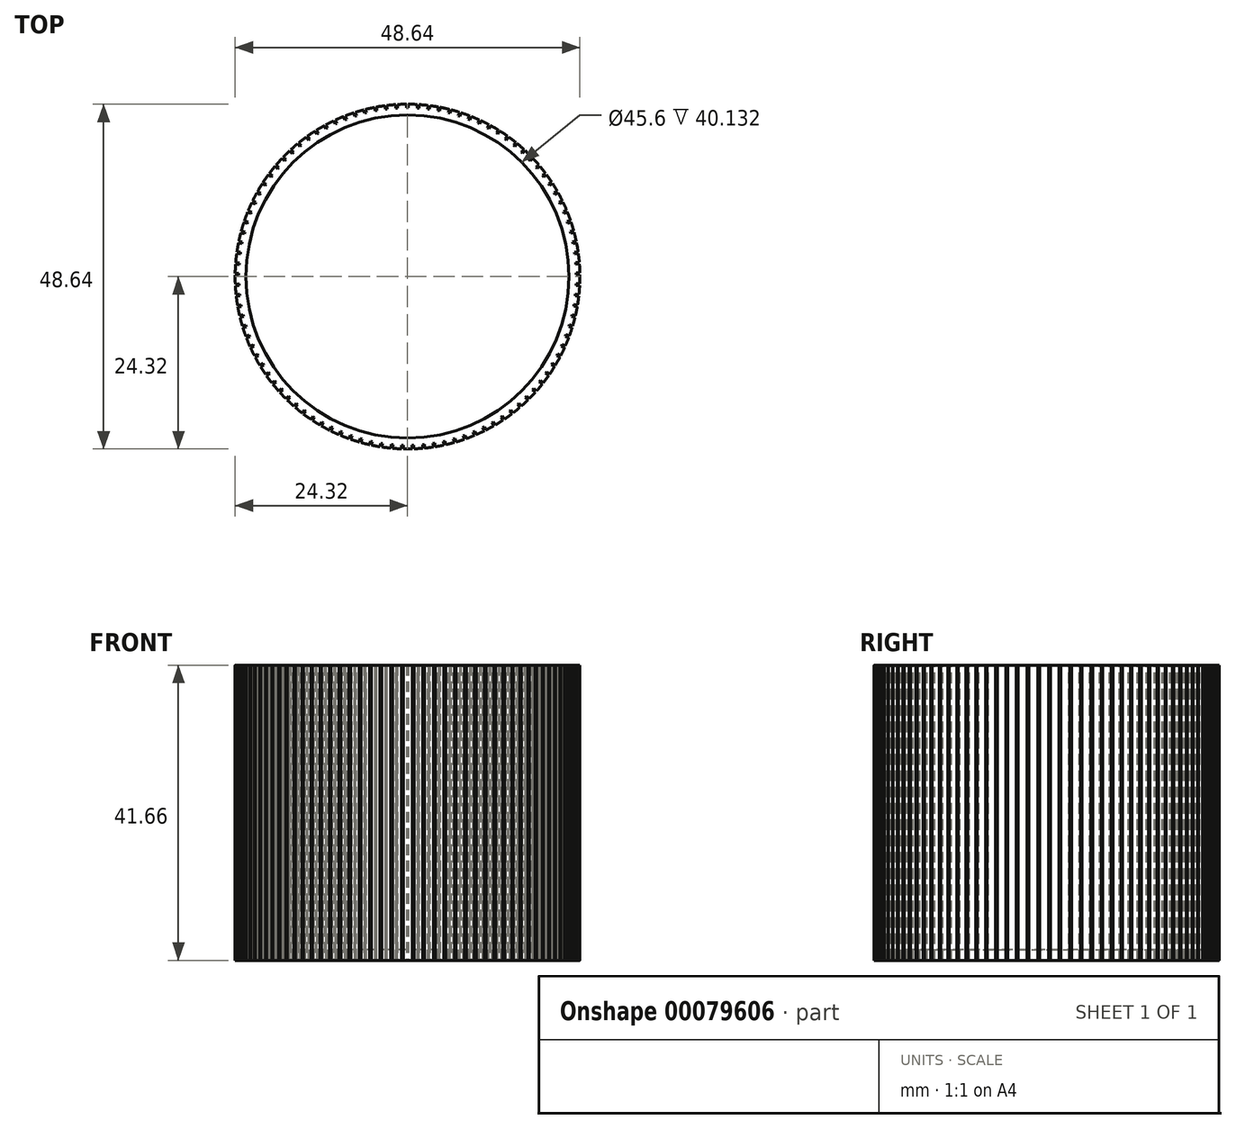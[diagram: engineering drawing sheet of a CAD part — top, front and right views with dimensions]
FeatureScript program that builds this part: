
annotation { "Feature Type Name" : "Feature", "Feature Type Description" : "" }
export const myFeature = defineFeature(function(context is Context, id is Id, definition is map)
    precondition{}
    {
        {
            var Q0;
            Q0=qCreatedBy(makeId("Top.planeOp"),FACE);
            var sketch = newSketch(context, id + "F0", { "sketchPlane" : qUnion([Q0])});
            skCircle(sketch, "E0", {"center": v(0, 0) * mm, "radius": 24.32 * mm});
            skSolve(sketch);
        }
        {
            var Q0;
            Q0 = qSketchRegion(id + "F0", true);
            extrude(context, id + "F1", {"entities" : qUnion([Q0]), "depth" : 41.66 * mm});
        }
        {
            var Q0;
            Q0=makeQuery(id+"F1.opExtrude","CAP_FACE",FACE,{"disambiguationData":[OSD([sQuery(id+"F0.wireOp",EDGE,"E0")])],"isStart":false});
            shell(context, id + "F2", {"entities" : qUnion([Q0]), "thickness" : 1.52 * mm});
        }
        {
            var Q0;
            Q0=makeQuery(id+"F1.opExtrude","CAP_FACE",FACE,{"disambiguationData":[OSD([sQuery(id+"F0.wireOp",EDGE,"E0")])],"isStart":false});
            var sketch = newSketch(context, id + "F3", { "sketchPlane" : qUnion([Q0])});
            skLineSegment(sketch, "E1.left", {"start": v(-0.13, 25.12) * mm, "end": v(-0.13, 23.82) * mm});
            skLineSegment(sketch, "E1.right", {"start": v(0.13, 25.12) * mm, "end": v(0.13, 23.82) * mm});
            skLineSegment(sketch, "E2.1.0", {"start": v(1.43, 25.08) * mm, "end": v(1.35, 23.78) * mm});
            skLineSegment(sketch, "E2.1.1", {"start": v(1.69, 25.07) * mm, "end": v(1.6, 23.76) * mm});
            skLineSegment(sketch, "E2.1.2", {"start": v(1.35, 23.78) * mm, "end": v(1.6, 23.76) * mm});
            skLineSegment(sketch, "E2.1.3", {"start": v(1.43, 25.08) * mm, "end": v(1.69, 25.07) * mm});
            skLineSegment(sketch, "E2.2.0", {"start": v(3, 24.94) * mm, "end": v(2.83, 23.65) * mm});
            skLineSegment(sketch, "E2.2.1", {"start": v(3.24, 24.91) * mm, "end": v(3.08, 23.62) * mm});
            skLineSegment(sketch, "E2.2.2", {"start": v(2.83, 23.65) * mm, "end": v(3.08, 23.62) * mm});
            skLineSegment(sketch, "E2.2.3", {"start": v(3, 24.94) * mm, "end": v(3.24, 24.91) * mm});
            skLineSegment(sketch, "E2.3.0", {"start": v(4.54, 24.7) * mm, "end": v(4.3, 23.43) * mm});
            skLineSegment(sketch, "E2.3.1", {"start": v(4.78, 24.66) * mm, "end": v(4.54, 23.38) * mm});
            skLineSegment(sketch, "E2.3.2", {"start": v(4.3, 23.43) * mm, "end": v(4.54, 23.38) * mm});
            skLineSegment(sketch, "E2.3.3", {"start": v(4.54, 24.7) * mm, "end": v(4.78, 24.66) * mm});
            skLineSegment(sketch, "E2.4.0", {"start": v(6.06, 24.38) * mm, "end": v(5.74, 23.11) * mm});
            skLineSegment(sketch, "E2.4.1", {"start": v(6.3, 24.32) * mm, "end": v(5.99, 23.05) * mm});
            skLineSegment(sketch, "E2.4.2", {"start": v(5.74, 23.11) * mm, "end": v(5.99, 23.05) * mm});
            skLineSegment(sketch, "E2.4.3", {"start": v(6.06, 24.38) * mm, "end": v(6.3, 24.32) * mm});
            skLineSegment(sketch, "E2.5.0", {"start": v(7.57, 23.96) * mm, "end": v(7.17, 22.71) * mm});
            skLineSegment(sketch, "E2.5.1", {"start": v(7.8, 23.88) * mm, "end": v(7.4, 22.63) * mm});
            skLineSegment(sketch, "E2.5.2", {"start": v(7.17, 22.71) * mm, "end": v(7.4, 22.63) * mm});
            skLineSegment(sketch, "E2.5.3", {"start": v(7.57, 23.96) * mm, "end": v(7.8, 23.88) * mm});
            skLineSegment(sketch, "E2.6.0", {"start": v(9.04, 23.44) * mm, "end": v(8.56, 22.22) * mm});
            skLineSegment(sketch, "E2.6.1", {"start": v(9.28, 23.35) * mm, "end": v(8.8, 22.13) * mm});
            skLineSegment(sketch, "E2.6.2", {"start": v(8.56, 22.22) * mm, "end": v(8.8, 22.13) * mm});
            skLineSegment(sketch, "E2.6.3", {"start": v(9.04, 23.44) * mm, "end": v(9.28, 23.35) * mm});
            skLineSegment(sketch, "E2.7.0", {"start": v(10.48, 22.83) * mm, "end": v(9.93, 21.65) * mm});
            skLineSegment(sketch, "E2.7.1", {"start": v(10.7, 22.73) * mm, "end": v(10.16, 21.54) * mm});
            skLineSegment(sketch, "E2.7.2", {"start": v(9.93, 21.65) * mm, "end": v(10.16, 21.54) * mm});
            skLineSegment(sketch, "E2.7.3", {"start": v(10.48, 22.83) * mm, "end": v(10.7, 22.73) * mm});
            skLineSegment(sketch, "E2.8.0", {"start": v(11.88, 22.14) * mm, "end": v(11.25, 20.99) * mm});
            skLineSegment(sketch, "E2.8.1", {"start": v(12.1, 22.02) * mm, "end": v(11.48, 20.87) * mm});
            skLineSegment(sketch, "E2.8.2", {"start": v(11.25, 20.99) * mm, "end": v(11.48, 20.87) * mm});
            skLineSegment(sketch, "E2.8.3", {"start": v(11.88, 22.14) * mm, "end": v(12.1, 22.02) * mm});
            skLineSegment(sketch, "E2.9.0", {"start": v(13.23, 21.36) * mm, "end": v(12.54, 20.25) * mm});
            skLineSegment(sketch, "E2.9.1", {"start": v(13.45, 21.22) * mm, "end": v(12.75, 20.11) * mm});
            skLineSegment(sketch, "E2.9.2", {"start": v(12.54, 20.25) * mm, "end": v(12.75, 20.11) * mm});
            skLineSegment(sketch, "E2.9.3", {"start": v(13.23, 21.36) * mm, "end": v(13.45, 21.22) * mm});
            skLineSegment(sketch, "E2.10.0", {"start": v(14.53, 20.5) * mm, "end": v(13.77, 19.43) * mm});
            skLineSegment(sketch, "E2.10.1", {"start": v(14.74, 20.34) * mm, "end": v(13.98, 19.28) * mm});
            skLineSegment(sketch, "E2.10.2", {"start": v(13.77, 19.43) * mm, "end": v(13.98, 19.28) * mm});
            skLineSegment(sketch, "E2.10.3", {"start": v(14.53, 20.5) * mm, "end": v(14.74, 20.34) * mm});
            skLineSegment(sketch, "E2.11.0", {"start": v(15.78, 19.55) * mm, "end": v(14.95, 18.54) * mm});
            skLineSegment(sketch, "E2.11.1", {"start": v(15.98, 19.39) * mm, "end": v(15.15, 18.38) * mm});
            skLineSegment(sketch, "E2.11.2", {"start": v(14.95, 18.54) * mm, "end": v(15.15, 18.38) * mm});
            skLineSegment(sketch, "E2.11.3", {"start": v(15.78, 19.55) * mm, "end": v(15.98, 19.39) * mm});
            skLineSegment(sketch, "E2.12.0", {"start": v(16.96, 18.53) * mm, "end": v(16.08, 17.57) * mm});
            skLineSegment(sketch, "E2.12.1", {"start": v(17.15, 18.36) * mm, "end": v(16.26, 17.4) * mm});
            skLineSegment(sketch, "E2.12.2", {"start": v(16.08, 17.57) * mm, "end": v(16.26, 17.4) * mm});
            skLineSegment(sketch, "E2.12.3", {"start": v(16.96, 18.53) * mm, "end": v(17.15, 18.36) * mm});
            skLineSegment(sketch, "E2.13.0", {"start": v(18.08, 17.44) * mm, "end": v(17.14, 16.54) * mm});
            skLineSegment(sketch, "E2.13.1", {"start": v(18.26, 17.26) * mm, "end": v(17.31, 16.35) * mm});
            skLineSegment(sketch, "E2.13.2", {"start": v(17.14, 16.54) * mm, "end": v(17.31, 16.35) * mm});
            skLineSegment(sketch, "E2.13.3", {"start": v(18.08, 17.44) * mm, "end": v(18.26, 17.26) * mm});
            skLineSegment(sketch, "E2.14.0", {"start": v(19.13, 16.28) * mm, "end": v(18.13, 15.44) * mm});
            skLineSegment(sketch, "E2.14.1", {"start": v(19.3, 16.09) * mm, "end": v(18.3, 15.25) * mm});
            skLineSegment(sketch, "E2.14.2", {"start": v(18.13, 15.44) * mm, "end": v(18.3, 15.25) * mm});
            skLineSegment(sketch, "E2.14.3", {"start": v(19.13, 16.28) * mm, "end": v(19.3, 16.09) * mm});
            skLineSegment(sketch, "E2.15.0", {"start": v(20.1, 15.06) * mm, "end": v(19.06, 14.28) * mm});
            skLineSegment(sketch, "E2.15.1", {"start": v(20.26, 14.86) * mm, "end": v(19.2, 14.08) * mm});
            skLineSegment(sketch, "E2.15.2", {"start": v(19.06, 14.28) * mm, "end": v(19.2, 14.08) * mm});
            skLineSegment(sketch, "E2.15.3", {"start": v(20.1, 15.06) * mm, "end": v(20.26, 14.86) * mm});
            skLineSegment(sketch, "E2.16.0", {"start": v(21, 13.78) * mm, "end": v(19.9, 13.07) * mm});
            skLineSegment(sketch, "E2.16.1", {"start": v(21.14, 13.57) * mm, "end": v(20.05, 12.86) * mm});
            skLineSegment(sketch, "E2.16.2", {"start": v(19.9, 13.07) * mm, "end": v(20.05, 12.86) * mm});
            skLineSegment(sketch, "E2.16.3", {"start": v(21, 13.78) * mm, "end": v(21.14, 13.57) * mm});
            skLineSegment(sketch, "E2.17.0", {"start": v(21.82, 12.45) * mm, "end": v(20.68, 11.8) * mm});
            skLineSegment(sketch, "E2.17.1", {"start": v(21.94, 12.23) * mm, "end": v(20.8, 11.59) * mm});
            skLineSegment(sketch, "E2.17.2", {"start": v(20.68, 11.8) * mm, "end": v(20.8, 11.59) * mm});
            skLineSegment(sketch, "E2.17.3", {"start": v(21.82, 12.45) * mm, "end": v(21.94, 12.23) * mm});
            skLineSegment(sketch, "E2.18.0", {"start": v(22.55, 11.07) * mm, "end": v(21.37, 10.5) * mm});
            skLineSegment(sketch, "E2.18.1", {"start": v(22.66, 10.84) * mm, "end": v(21.49, 10.27) * mm});
            skLineSegment(sketch, "E2.18.2", {"start": v(21.37, 10.5) * mm, "end": v(21.49, 10.27) * mm});
            skLineSegment(sketch, "E2.18.3", {"start": v(22.55, 11.07) * mm, "end": v(22.66, 10.84) * mm});
            skLineSegment(sketch, "E2.19.0", {"start": v(23.2, 9.65) * mm, "end": v(21.99, 9.15) * mm});
            skLineSegment(sketch, "E2.19.1", {"start": v(23.3, 9.41) * mm, "end": v(22.08, 8.92) * mm});
            skLineSegment(sketch, "E2.19.2", {"start": v(21.99, 9.15) * mm, "end": v(22.08, 8.92) * mm});
            skLineSegment(sketch, "E2.19.3", {"start": v(23.2, 9.65) * mm, "end": v(23.3, 9.41) * mm});
            skLineSegment(sketch, "E2.20.0", {"start": v(23.75, 8.19) * mm, "end": v(22.51, 7.77) * mm});
            skLineSegment(sketch, "E2.20.1", {"start": v(23.83, 7.95) * mm, "end": v(22.6, 7.53) * mm});
            skLineSegment(sketch, "E2.20.2", {"start": v(22.51, 7.77) * mm, "end": v(22.6, 7.53) * mm});
            skLineSegment(sketch, "E2.20.3", {"start": v(23.75, 8.19) * mm, "end": v(23.83, 7.95) * mm});
            skLineSegment(sketch, "E2.21.0", {"start": v(24.21, 6.7) * mm, "end": v(22.95, 6.35) * mm});
            skLineSegment(sketch, "E2.21.1", {"start": v(24.28, 6.45) * mm, "end": v(23.02, 6.1) * mm});
            skLineSegment(sketch, "E2.21.2", {"start": v(22.95, 6.35) * mm, "end": v(23.02, 6.1) * mm});
            skLineSegment(sketch, "E2.21.3", {"start": v(24.21, 6.7) * mm, "end": v(24.28, 6.45) * mm});
            skLineSegment(sketch, "E2.22.0", {"start": v(24.58, 5.18) * mm, "end": v(23.3, 4.92) * mm});
            skLineSegment(sketch, "E2.22.1", {"start": v(24.63, 4.93) * mm, "end": v(23.35, 4.67) * mm});
            skLineSegment(sketch, "E2.22.2", {"start": v(23.3, 4.92) * mm, "end": v(23.35, 4.67) * mm});
            skLineSegment(sketch, "E2.22.3", {"start": v(24.58, 5.18) * mm, "end": v(24.63, 4.93) * mm});
            skLineSegment(sketch, "E2.23.0", {"start": v(24.86, 3.64) * mm, "end": v(23.56, 3.46) * mm});
            skLineSegment(sketch, "E2.23.1", {"start": v(24.9, 3.39) * mm, "end": v(23.6, 3.2) * mm});
            skLineSegment(sketch, "E2.23.2", {"start": v(23.56, 3.46) * mm, "end": v(23.6, 3.2) * mm});
            skLineSegment(sketch, "E2.23.3", {"start": v(24.86, 3.64) * mm, "end": v(24.9, 3.39) * mm});
            skLineSegment(sketch, "E2.24.0", {"start": v(25.04, 2.09) * mm, "end": v(23.73, 1.99) * mm});
            skLineSegment(sketch, "E2.24.1", {"start": v(25.06, 1.84) * mm, "end": v(23.75, 1.73) * mm});
            skLineSegment(sketch, "E2.24.2", {"start": v(23.73, 1.99) * mm, "end": v(23.75, 1.73) * mm});
            skLineSegment(sketch, "E2.24.3", {"start": v(25.04, 2.09) * mm, "end": v(25.06, 1.84) * mm});
            skLineSegment(sketch, "E2.25.0", {"start": v(25.12, 0.53) * mm, "end": v(23.8, 0.5) * mm});
            skLineSegment(sketch, "E2.25.1", {"start": v(25.12, 0.27) * mm, "end": v(23.81, 0.25) * mm});
            skLineSegment(sketch, "E2.25.2", {"start": v(23.8, 0.5) * mm, "end": v(23.81, 0.25) * mm});
            skLineSegment(sketch, "E2.25.3", {"start": v(25.12, 0.53) * mm, "end": v(25.12, 0.27) * mm});
            skLineSegment(sketch, "E2.26.0", {"start": v(25.1, -1.03) * mm, "end": v(23.8, -0.97) * mm});
            skLineSegment(sketch, "E2.26.1", {"start": v(25.09, -1.29) * mm, "end": v(23.78, -1.23) * mm});
            skLineSegment(sketch, "E2.26.2", {"start": v(23.8, -0.97) * mm, "end": v(23.78, -1.23) * mm});
            skLineSegment(sketch, "E2.26.3", {"start": v(25.1, -1.03) * mm, "end": v(25.09, -1.29) * mm});
            skLineSegment(sketch, "E2.27.0", {"start": v(24.99, -2.6) * mm, "end": v(23.69, -2.45) * mm});
            skLineSegment(sketch, "E2.27.1", {"start": v(24.96, -2.84) * mm, "end": v(23.66, -2.7) * mm});
            skLineSegment(sketch, "E2.27.2", {"start": v(23.69, -2.45) * mm, "end": v(23.66, -2.7) * mm});
            skLineSegment(sketch, "E2.27.3", {"start": v(24.99, -2.6) * mm, "end": v(24.96, -2.84) * mm});
            skLineSegment(sketch, "E2.28.0", {"start": v(24.78, -4.14) * mm, "end": v(23.5, -3.92) * mm});
            skLineSegment(sketch, "E2.28.1", {"start": v(24.74, -4.4) * mm, "end": v(23.45, -4.17) * mm});
            skLineSegment(sketch, "E2.28.2", {"start": v(23.5, -3.92) * mm, "end": v(23.45, -4.17) * mm});
            skLineSegment(sketch, "E2.28.3", {"start": v(24.78, -4.14) * mm, "end": v(24.74, -4.4) * mm});
            skLineSegment(sketch, "E2.29.0", {"start": v(24.47, -5.67) * mm, "end": v(23.2, -5.37) * mm});
            skLineSegment(sketch, "E2.29.1", {"start": v(24.42, -5.92) * mm, "end": v(23.14, -5.62) * mm});
            skLineSegment(sketch, "E2.29.2", {"start": v(23.2, -5.37) * mm, "end": v(23.14, -5.62) * mm});
            skLineSegment(sketch, "E2.29.3", {"start": v(24.47, -5.67) * mm, "end": v(24.42, -5.92) * mm});
            skLineSegment(sketch, "E2.30.0", {"start": v(24.07, -7.18) * mm, "end": v(22.82, -6.8) * mm});
            skLineSegment(sketch, "E2.30.1", {"start": v(24, -7.43) * mm, "end": v(22.75, -7.04) * mm});
            skLineSegment(sketch, "E2.30.2", {"start": v(22.82, -6.8) * mm, "end": v(22.75, -7.04) * mm});
            skLineSegment(sketch, "E2.30.3", {"start": v(24.07, -7.18) * mm, "end": v(24, -7.43) * mm});
            skLineSegment(sketch, "E2.31.0", {"start": v(23.58, -8.66) * mm, "end": v(22.36, -8.2) * mm});
            skLineSegment(sketch, "E2.31.1", {"start": v(23.5, -8.9) * mm, "end": v(22.27, -8.45) * mm});
            skLineSegment(sketch, "E2.31.2", {"start": v(22.36, -8.2) * mm, "end": v(22.27, -8.45) * mm});
            skLineSegment(sketch, "E2.31.3", {"start": v(23.58, -8.66) * mm, "end": v(23.5, -8.9) * mm});
            skLineSegment(sketch, "E2.32.0", {"start": v(23, -10.11) * mm, "end": v(21.8, -9.58) * mm});
            skLineSegment(sketch, "E2.32.1", {"start": v(22.9, -10.35) * mm, "end": v(21.7, -9.81) * mm});
            skLineSegment(sketch, "E2.32.2", {"start": v(21.8, -9.58) * mm, "end": v(21.7, -9.81) * mm});
            skLineSegment(sketch, "E2.32.3", {"start": v(23, -10.11) * mm, "end": v(22.9, -10.35) * mm});
            skLineSegment(sketch, "E2.33.0", {"start": v(22.32, -11.52) * mm, "end": v(21.17, -10.92) * mm});
            skLineSegment(sketch, "E2.33.1", {"start": v(22.2, -11.75) * mm, "end": v(21.05, -11.14) * mm});
            skLineSegment(sketch, "E2.33.2", {"start": v(21.17, -10.92) * mm, "end": v(21.05, -11.14) * mm});
            skLineSegment(sketch, "E2.33.3", {"start": v(22.32, -11.52) * mm, "end": v(22.2, -11.75) * mm});
            skLineSegment(sketch, "E2.34.0", {"start": v(21.56, -12.89) * mm, "end": v(20.45, -12.21) * mm});
            skLineSegment(sketch, "E2.34.1", {"start": v(21.43, -13.1) * mm, "end": v(20.31, -12.43) * mm});
            skLineSegment(sketch, "E2.34.2", {"start": v(20.45, -12.21) * mm, "end": v(20.31, -12.43) * mm});
            skLineSegment(sketch, "E2.34.3", {"start": v(21.56, -12.89) * mm, "end": v(21.43, -13.1) * mm});
            skLineSegment(sketch, "E2.35.0", {"start": v(20.72, -14.2) * mm, "end": v(19.65, -13.46) * mm});
            skLineSegment(sketch, "E2.35.1", {"start": v(20.58, -14.41) * mm, "end": v(19.5, -13.67) * mm});
            skLineSegment(sketch, "E2.35.2", {"start": v(19.65, -13.46) * mm, "end": v(19.5, -13.67) * mm});
            skLineSegment(sketch, "E2.35.3", {"start": v(20.72, -14.2) * mm, "end": v(20.58, -14.41) * mm});
            skLineSegment(sketch, "E2.36.0", {"start": v(19.8, -15.46) * mm, "end": v(18.77, -14.65) * mm});
            skLineSegment(sketch, "E2.36.1", {"start": v(19.64, -15.66) * mm, "end": v(18.62, -14.85) * mm});
            skLineSegment(sketch, "E2.36.2", {"start": v(18.77, -14.65) * mm, "end": v(18.62, -14.85) * mm});
            skLineSegment(sketch, "E2.36.3", {"start": v(19.8, -15.46) * mm, "end": v(19.64, -15.66) * mm});
            skLineSegment(sketch, "E2.37.0", {"start": v(18.8, -16.66) * mm, "end": v(17.83, -15.8) * mm});
            skLineSegment(sketch, "E2.37.1", {"start": v(18.63, -16.85) * mm, "end": v(17.66, -15.98) * mm});
            skLineSegment(sketch, "E2.37.2", {"start": v(17.83, -15.8) * mm, "end": v(17.66, -15.98) * mm});
            skLineSegment(sketch, "E2.37.3", {"start": v(18.8, -16.66) * mm, "end": v(18.63, -16.85) * mm});
            skLineSegment(sketch, "E2.38.0", {"start": v(17.73, -17.8) * mm, "end": v(16.8, -16.87) * mm});
            skLineSegment(sketch, "E2.38.1", {"start": v(17.55, -17.98) * mm, "end": v(16.63, -17.05) * mm});
            skLineSegment(sketch, "E2.38.2", {"start": v(16.8, -16.87) * mm, "end": v(16.63, -17.05) * mm});
            skLineSegment(sketch, "E2.38.3", {"start": v(17.73, -17.8) * mm, "end": v(17.55, -17.98) * mm});
            skLineSegment(sketch, "E2.39.0", {"start": v(16.59, -18.87) * mm, "end": v(15.73, -17.88) * mm});
            skLineSegment(sketch, "E2.39.1", {"start": v(16.4, -19.04) * mm, "end": v(15.54, -18.05) * mm});
            skLineSegment(sketch, "E2.39.2", {"start": v(15.73, -17.88) * mm, "end": v(15.54, -18.05) * mm});
            skLineSegment(sketch, "E2.39.3", {"start": v(16.59, -18.87) * mm, "end": v(16.4, -19.04) * mm});
            skLineSegment(sketch, "E2.40.0", {"start": v(15.38, -19.86) * mm, "end": v(14.59, -18.83) * mm});
            skLineSegment(sketch, "E2.40.1", {"start": v(15.18, -20.02) * mm, "end": v(14.39, -18.98) * mm});
            skLineSegment(sketch, "E2.40.2", {"start": v(14.59, -18.83) * mm, "end": v(14.39, -18.98) * mm});
            skLineSegment(sketch, "E2.40.3", {"start": v(15.38, -19.86) * mm, "end": v(15.18, -20.02) * mm});
            skLineSegment(sketch, "E2.41.0", {"start": v(14.12, -20.78) * mm, "end": v(13.39, -19.7) * mm});
            skLineSegment(sketch, "E2.41.1", {"start": v(13.9, -20.92) * mm, "end": v(13.18, -19.84) * mm});
            skLineSegment(sketch, "E2.41.2", {"start": v(13.39, -19.7) * mm, "end": v(13.18, -19.84) * mm});
            skLineSegment(sketch, "E2.41.3", {"start": v(14.12, -20.78) * mm, "end": v(13.9, -20.92) * mm});
            skLineSegment(sketch, "E2.42.0", {"start": v(12.8, -21.62) * mm, "end": v(12.14, -20.49) * mm});
            skLineSegment(sketch, "E2.42.1", {"start": v(12.58, -21.75) * mm, "end": v(11.92, -20.62) * mm});
            skLineSegment(sketch, "E2.42.2", {"start": v(12.14, -20.49) * mm, "end": v(11.92, -20.62) * mm});
            skLineSegment(sketch, "E2.42.3", {"start": v(12.8, -21.62) * mm, "end": v(12.58, -21.75) * mm});
            skLineSegment(sketch, "E2.43.0", {"start": v(11.43, -22.37) * mm, "end": v(10.84, -21.2) * mm});
            skLineSegment(sketch, "E2.43.1", {"start": v(11.2, -22.49) * mm, "end": v(10.62, -21.32) * mm});
            skLineSegment(sketch, "E2.43.2", {"start": v(10.84, -21.2) * mm, "end": v(10.62, -21.32) * mm});
            skLineSegment(sketch, "E2.43.3", {"start": v(11.43, -22.37) * mm, "end": v(11.2, -22.49) * mm});
            skLineSegment(sketch, "E2.44.0", {"start": v(10.02, -23.04) * mm, "end": v(9.5, -21.84) * mm});
            skLineSegment(sketch, "E2.44.1", {"start": v(9.78, -23.14) * mm, "end": v(9.27, -21.94) * mm});
            skLineSegment(sketch, "E2.44.2", {"start": v(9.5, -21.84) * mm, "end": v(9.27, -21.94) * mm});
            skLineSegment(sketch, "E2.44.3", {"start": v(10.02, -23.04) * mm, "end": v(9.78, -23.14) * mm});
            skLineSegment(sketch, "E2.45.0", {"start": v(8.57, -23.62) * mm, "end": v(8.13, -22.39) * mm});
            skLineSegment(sketch, "E2.45.1", {"start": v(8.33, -23.7) * mm, "end": v(7.89, -22.47) * mm});
            skLineSegment(sketch, "E2.45.2", {"start": v(8.13, -22.39) * mm, "end": v(7.89, -22.47) * mm});
            skLineSegment(sketch, "E2.45.3", {"start": v(8.57, -23.62) * mm, "end": v(8.33, -23.7) * mm});
            skLineSegment(sketch, "E2.46.0", {"start": v(7.08, -24.1) * mm, "end": v(6.72, -22.85) * mm});
            skLineSegment(sketch, "E2.46.1", {"start": v(6.84, -24.17) * mm, "end": v(6.48, -22.92) * mm});
            skLineSegment(sketch, "E2.46.2", {"start": v(6.72, -22.85) * mm, "end": v(6.48, -22.92) * mm});
            skLineSegment(sketch, "E2.46.3", {"start": v(7.08, -24.1) * mm, "end": v(6.84, -24.17) * mm});
            skLineSegment(sketch, "E2.47.0", {"start": v(5.57, -24.5) * mm, "end": v(5.29, -23.22) * mm});
            skLineSegment(sketch, "E2.47.1", {"start": v(5.32, -24.55) * mm, "end": v(5.04, -23.28) * mm});
            skLineSegment(sketch, "E2.47.2", {"start": v(5.29, -23.22) * mm, "end": v(5.04, -23.28) * mm});
            skLineSegment(sketch, "E2.47.3", {"start": v(5.57, -24.5) * mm, "end": v(5.32, -24.55) * mm});
            skLineSegment(sketch, "E2.48.0", {"start": v(4.04, -24.8) * mm, "end": v(3.83, -23.5) * mm});
            skLineSegment(sketch, "E2.48.1", {"start": v(3.79, -24.84) * mm, "end": v(3.58, -23.54) * mm});
            skLineSegment(sketch, "E2.48.2", {"start": v(3.83, -23.5) * mm, "end": v(3.58, -23.54) * mm});
            skLineSegment(sketch, "E2.48.3", {"start": v(4.04, -24.8) * mm, "end": v(3.79, -24.84) * mm});
            skLineSegment(sketch, "E2.49.0", {"start": v(2.49, -25) * mm, "end": v(2.37, -23.7) * mm});
            skLineSegment(sketch, "E2.49.1", {"start": v(2.24, -25.02) * mm, "end": v(2.11, -23.72) * mm});
            skLineSegment(sketch, "E2.49.2", {"start": v(2.37, -23.7) * mm, "end": v(2.11, -23.72) * mm});
            skLineSegment(sketch, "E2.49.3", {"start": v(2.49, -25) * mm, "end": v(2.24, -25.02) * mm});
            skLineSegment(sketch, "E2.50.0", {"start": v(0.93, -25.1) * mm, "end": v(0.89, -23.8) * mm});
            skLineSegment(sketch, "E2.50.1", {"start": v(0.68, -25.11) * mm, "end": v(0.63, -23.8) * mm});
            skLineSegment(sketch, "E2.50.2", {"start": v(0.89, -23.8) * mm, "end": v(0.63, -23.8) * mm});
            skLineSegment(sketch, "E2.50.3", {"start": v(0.93, -25.1) * mm, "end": v(0.68, -25.11) * mm});
            skLineSegment(sketch, "E2.51.0", {"start": v(-0.63, -25.11) * mm, "end": v(-0.6, -23.8) * mm});
            skLineSegment(sketch, "E2.51.1", {"start": v(-0.89, -25.1) * mm, "end": v(-0.85, -23.8) * mm});
            skLineSegment(sketch, "E2.51.2", {"start": v(-0.6, -23.8) * mm, "end": v(-0.85, -23.8) * mm});
            skLineSegment(sketch, "E2.51.3", {"start": v(-0.63, -25.11) * mm, "end": v(-0.89, -25.1) * mm});
            skLineSegment(sketch, "E2.52.0", {"start": v(-2.2, -25.03) * mm, "end": v(-2.07, -23.73) * mm});
            skLineSegment(sketch, "E2.52.1", {"start": v(-2.44, -25) * mm, "end": v(-2.32, -23.7) * mm});
            skLineSegment(sketch, "E2.52.2", {"start": v(-2.07, -23.73) * mm, "end": v(-2.32, -23.7) * mm});
            skLineSegment(sketch, "E2.52.3", {"start": v(-2.2, -25.03) * mm, "end": v(-2.44, -25) * mm});
            skLineSegment(sketch, "E2.53.0", {"start": v(-3.74, -24.84) * mm, "end": v(-3.54, -23.55) * mm});
            skLineSegment(sketch, "E2.53.1", {"start": v(-4, -24.8) * mm, "end": v(-3.8, -23.51) * mm});
            skLineSegment(sketch, "E2.53.2", {"start": v(-3.54, -23.55) * mm, "end": v(-3.8, -23.51) * mm});
            skLineSegment(sketch, "E2.53.3", {"start": v(-3.74, -24.84) * mm, "end": v(-4, -24.8) * mm});
            skLineSegment(sketch, "E2.54.0", {"start": v(-5.28, -24.56) * mm, "end": v(-5, -23.28) * mm});
            skLineSegment(sketch, "E2.54.1", {"start": v(-5.53, -24.5) * mm, "end": v(-5.25, -23.23) * mm});
            skLineSegment(sketch, "E2.54.2", {"start": v(-5, -23.28) * mm, "end": v(-5.25, -23.23) * mm});
            skLineSegment(sketch, "E2.54.3", {"start": v(-5.28, -24.56) * mm, "end": v(-5.53, -24.5) * mm});
            skLineSegment(sketch, "E2.55.0", {"start": v(-6.8, -24.19) * mm, "end": v(-6.44, -22.93) * mm});
            skLineSegment(sketch, "E2.55.1", {"start": v(-7.04, -24.12) * mm, "end": v(-6.68, -22.86) * mm});
            skLineSegment(sketch, "E2.55.2", {"start": v(-6.44, -22.93) * mm, "end": v(-6.68, -22.86) * mm});
            skLineSegment(sketch, "E2.55.3", {"start": v(-6.8, -24.19) * mm, "end": v(-7.04, -24.12) * mm});
            skLineSegment(sketch, "E2.56.0", {"start": v(-8.29, -23.72) * mm, "end": v(-7.85, -22.48) * mm});
            skLineSegment(sketch, "E2.56.1", {"start": v(-8.53, -23.63) * mm, "end": v(-8.09, -22.4) * mm});
            skLineSegment(sketch, "E2.56.2", {"start": v(-7.85, -22.48) * mm, "end": v(-8.09, -22.4) * mm});
            skLineSegment(sketch, "E2.56.3", {"start": v(-8.29, -23.72) * mm, "end": v(-8.53, -23.63) * mm});
            skLineSegment(sketch, "E2.57.0", {"start": v(-9.74, -23.16) * mm, "end": v(-9.23, -21.95) * mm});
            skLineSegment(sketch, "E2.57.1", {"start": v(-9.98, -23.06) * mm, "end": v(-9.46, -21.85) * mm});
            skLineSegment(sketch, "E2.57.2", {"start": v(-9.23, -21.95) * mm, "end": v(-9.46, -21.85) * mm});
            skLineSegment(sketch, "E2.57.3", {"start": v(-9.74, -23.16) * mm, "end": v(-9.98, -23.06) * mm});
            skLineSegment(sketch, "E2.58.0", {"start": v(-11.16, -22.5) * mm, "end": v(-10.58, -21.34) * mm});
            skLineSegment(sketch, "E2.58.1", {"start": v(-11.4, -22.4) * mm, "end": v(-10.8, -21.22) * mm});
            skLineSegment(sketch, "E2.58.2", {"start": v(-10.58, -21.34) * mm, "end": v(-10.8, -21.22) * mm});
            skLineSegment(sketch, "E2.58.3", {"start": v(-11.16, -22.5) * mm, "end": v(-11.4, -22.4) * mm});
            skLineSegment(sketch, "E2.59.0", {"start": v(-12.54, -21.77) * mm, "end": v(-11.88, -20.64) * mm});
            skLineSegment(sketch, "E2.59.1", {"start": v(-12.76, -21.64) * mm, "end": v(-12.1, -20.51) * mm});
            skLineSegment(sketch, "E2.59.2", {"start": v(-11.88, -20.64) * mm, "end": v(-12.1, -20.51) * mm});
            skLineSegment(sketch, "E2.59.3", {"start": v(-12.54, -21.77) * mm, "end": v(-12.76, -21.64) * mm});
            skLineSegment(sketch, "E2.60.0", {"start": v(-13.87, -20.95) * mm, "end": v(-13.14, -19.86) * mm});
            skLineSegment(sketch, "E2.60.1", {"start": v(-14.08, -20.8) * mm, "end": v(-13.35, -19.72) * mm});
            skLineSegment(sketch, "E2.60.2", {"start": v(-13.14, -19.86) * mm, "end": v(-13.35, -19.72) * mm});
            skLineSegment(sketch, "E2.60.3", {"start": v(-13.87, -20.95) * mm, "end": v(-14.08, -20.8) * mm});
            skLineSegment(sketch, "E2.61.0", {"start": v(-15.15, -20.04) * mm, "end": v(-14.35, -19) * mm});
            skLineSegment(sketch, "E2.61.1", {"start": v(-15.35, -19.89) * mm, "end": v(-14.55, -18.85) * mm});
            skLineSegment(sketch, "E2.61.2", {"start": v(-14.35, -19) * mm, "end": v(-14.55, -18.85) * mm});
            skLineSegment(sketch, "E2.61.3", {"start": v(-15.15, -20.04) * mm, "end": v(-15.35, -19.89) * mm});
            skLineSegment(sketch, "E2.62.0", {"start": v(-16.36, -19.06) * mm, "end": v(-15.5, -18.08) * mm});
            skLineSegment(sketch, "E2.62.1", {"start": v(-16.55, -18.9) * mm, "end": v(-15.7, -17.9) * mm});
            skLineSegment(sketch, "E2.62.2", {"start": v(-15.5, -18.08) * mm, "end": v(-15.7, -17.9) * mm});
            skLineSegment(sketch, "E2.62.3", {"start": v(-16.36, -19.06) * mm, "end": v(-16.55, -18.9) * mm});
            skLineSegment(sketch, "E2.63.0", {"start": v(-17.52, -18) * mm, "end": v(-16.6, -17.08) * mm});
            skLineSegment(sketch, "E2.63.1", {"start": v(-17.7, -17.83) * mm, "end": v(-16.78, -16.9) * mm});
            skLineSegment(sketch, "E2.63.2", {"start": v(-16.6, -17.08) * mm, "end": v(-16.78, -16.9) * mm});
            skLineSegment(sketch, "E2.63.3", {"start": v(-17.52, -18) * mm, "end": v(-17.7, -17.83) * mm});
            skLineSegment(sketch, "E2.64.0", {"start": v(-18.6, -16.89) * mm, "end": v(-17.63, -16.01) * mm});
            skLineSegment(sketch, "E2.64.1", {"start": v(-18.77, -16.7) * mm, "end": v(-17.8, -15.82) * mm});
            skLineSegment(sketch, "E2.64.2", {"start": v(-17.63, -16.01) * mm, "end": v(-17.8, -15.82) * mm});
            skLineSegment(sketch, "E2.64.3", {"start": v(-18.6, -16.89) * mm, "end": v(-18.77, -16.7) * mm});
            skLineSegment(sketch, "E2.65.0", {"start": v(-19.61, -15.7) * mm, "end": v(-18.59, -14.89) * mm});
            skLineSegment(sketch, "E2.65.1", {"start": v(-19.77, -15.5) * mm, "end": v(-18.75, -14.69) * mm});
            skLineSegment(sketch, "E2.65.2", {"start": v(-18.59, -14.89) * mm, "end": v(-18.75, -14.69) * mm});
            skLineSegment(sketch, "E2.65.3", {"start": v(-19.61, -15.7) * mm, "end": v(-19.77, -15.5) * mm});
            skLineSegment(sketch, "E2.66.0", {"start": v(-20.55, -14.45) * mm, "end": v(-19.48, -13.7) * mm});
            skLineSegment(sketch, "E2.66.1", {"start": v(-20.7, -14.24) * mm, "end": v(-19.62, -13.5) * mm});
            skLineSegment(sketch, "E2.66.2", {"start": v(-19.48, -13.7) * mm, "end": v(-19.62, -13.5) * mm});
            skLineSegment(sketch, "E2.66.3", {"start": v(-20.55, -14.45) * mm, "end": v(-20.7, -14.24) * mm});
            skLineSegment(sketch, "E2.67.0", {"start": v(-21.41, -13.14) * mm, "end": v(-20.3, -12.46) * mm});
            skLineSegment(sketch, "E2.67.1", {"start": v(-21.54, -12.93) * mm, "end": v(-20.42, -12.25) * mm});
            skLineSegment(sketch, "E2.67.2", {"start": v(-20.3, -12.46) * mm, "end": v(-20.42, -12.25) * mm});
            skLineSegment(sketch, "E2.67.3", {"start": v(-21.41, -13.14) * mm, "end": v(-21.54, -12.93) * mm});
            skLineSegment(sketch, "E2.68.0", {"start": v(-22.19, -11.79) * mm, "end": v(-21.03, -11.18) * mm});
            skLineSegment(sketch, "E2.68.1", {"start": v(-22.3, -11.56) * mm, "end": v(-21.15, -10.95) * mm});
            skLineSegment(sketch, "E2.68.2", {"start": v(-21.03, -11.18) * mm, "end": v(-21.15, -10.95) * mm});
            skLineSegment(sketch, "E2.68.3", {"start": v(-22.19, -11.79) * mm, "end": v(-22.3, -11.56) * mm});
            skLineSegment(sketch, "E2.69.0", {"start": v(-22.88, -10.39) * mm, "end": v(-21.68, -9.85) * mm});
            skLineSegment(sketch, "E2.69.1", {"start": v(-22.98, -10.15) * mm, "end": v(-21.79, -9.62) * mm});
            skLineSegment(sketch, "E2.69.2", {"start": v(-21.68, -9.85) * mm, "end": v(-21.79, -9.62) * mm});
            skLineSegment(sketch, "E2.69.3", {"start": v(-22.88, -10.39) * mm, "end": v(-22.98, -10.15) * mm});
            skLineSegment(sketch, "E2.70.0", {"start": v(-23.48, -8.94) * mm, "end": v(-22.25, -8.48) * mm});
            skLineSegment(sketch, "E2.70.1", {"start": v(-23.57, -8.7) * mm, "end": v(-22.34, -8.25) * mm});
            skLineSegment(sketch, "E2.70.2", {"start": v(-22.25, -8.48) * mm, "end": v(-22.34, -8.25) * mm});
            skLineSegment(sketch, "E2.70.3", {"start": v(-23.48, -8.94) * mm, "end": v(-23.57, -8.7) * mm});
            skLineSegment(sketch, "E2.71.0", {"start": v(-23.99, -7.47) * mm, "end": v(-22.74, -7.08) * mm});
            skLineSegment(sketch, "E2.71.1", {"start": v(-24.06, -7.22) * mm, "end": v(-22.81, -6.84) * mm});
            skLineSegment(sketch, "E2.71.2", {"start": v(-22.74, -7.08) * mm, "end": v(-22.81, -6.84) * mm});
            skLineSegment(sketch, "E2.71.3", {"start": v(-23.99, -7.47) * mm, "end": v(-24.06, -7.22) * mm});
            skLineSegment(sketch, "E2.72.0", {"start": v(-24.4, -5.96) * mm, "end": v(-23.13, -5.66) * mm});
            skLineSegment(sketch, "E2.72.1", {"start": v(-24.46, -5.71) * mm, "end": v(-23.2, -5.41) * mm});
            skLineSegment(sketch, "E2.72.2", {"start": v(-23.13, -5.66) * mm, "end": v(-23.2, -5.41) * mm});
            skLineSegment(sketch, "E2.72.3", {"start": v(-24.4, -5.96) * mm, "end": v(-24.46, -5.71) * mm});
            skLineSegment(sketch, "E2.73.0", {"start": v(-24.73, -4.43) * mm, "end": v(-23.44, -4.2) * mm});
            skLineSegment(sketch, "E2.73.1", {"start": v(-24.77, -4.18) * mm, "end": v(-23.48, -3.96) * mm});
            skLineSegment(sketch, "E2.73.2", {"start": v(-23.44, -4.2) * mm, "end": v(-23.48, -3.96) * mm});
            skLineSegment(sketch, "E2.73.3", {"start": v(-24.73, -4.43) * mm, "end": v(-24.77, -4.18) * mm});
            skLineSegment(sketch, "E2.74.0", {"start": v(-24.96, -2.89) * mm, "end": v(-23.66, -2.74) * mm});
            skLineSegment(sketch, "E2.74.1", {"start": v(-24.98, -2.64) * mm, "end": v(-23.68, -2.5) * mm});
            skLineSegment(sketch, "E2.74.2", {"start": v(-23.66, -2.74) * mm, "end": v(-23.68, -2.5) * mm});
            skLineSegment(sketch, "E2.74.3", {"start": v(-24.96, -2.89) * mm, "end": v(-24.98, -2.64) * mm});
            skLineSegment(sketch, "E2.75.0", {"start": v(-25.09, -1.33) * mm, "end": v(-23.78, -1.27) * mm});
            skLineSegment(sketch, "E2.75.1", {"start": v(-25.1, -1.08) * mm, "end": v(-23.8, -1.01) * mm});
            skLineSegment(sketch, "E2.75.2", {"start": v(-23.78, -1.27) * mm, "end": v(-23.8, -1.01) * mm});
            skLineSegment(sketch, "E2.75.3", {"start": v(-25.09, -1.33) * mm, "end": v(-25.1, -1.08) * mm});
            skLineSegment(sketch, "E2.76.0", {"start": v(-25.12, 0.23) * mm, "end": v(-23.81, 0.21) * mm});
            skLineSegment(sketch, "E2.76.1", {"start": v(-25.12, 0.48) * mm, "end": v(-23.81, 0.47) * mm});
            skLineSegment(sketch, "E2.76.2", {"start": v(-23.81, 0.21) * mm, "end": v(-23.81, 0.47) * mm});
            skLineSegment(sketch, "E2.76.3", {"start": v(-25.12, 0.23) * mm, "end": v(-25.12, 0.48) * mm});
            skLineSegment(sketch, "E2.77.0", {"start": v(-25.06, 1.8) * mm, "end": v(-23.76, 1.7) * mm});
            skLineSegment(sketch, "E2.77.1", {"start": v(-25.04, 2.04) * mm, "end": v(-23.74, 1.95) * mm});
            skLineSegment(sketch, "E2.77.2", {"start": v(-23.76, 1.7) * mm, "end": v(-23.74, 1.95) * mm});
            skLineSegment(sketch, "E2.77.3", {"start": v(-25.06, 1.8) * mm, "end": v(-25.04, 2.04) * mm});
            skLineSegment(sketch, "E2.78.0", {"start": v(-24.9, 3.35) * mm, "end": v(-23.6, 3.16) * mm});
            skLineSegment(sketch, "E2.78.1", {"start": v(-24.86, 3.6) * mm, "end": v(-23.57, 3.42) * mm});
            skLineSegment(sketch, "E2.78.2", {"start": v(-23.6, 3.16) * mm, "end": v(-23.57, 3.42) * mm});
            skLineSegment(sketch, "E2.78.3", {"start": v(-24.9, 3.35) * mm, "end": v(-24.86, 3.6) * mm});
            skLineSegment(sketch, "E2.79.0", {"start": v(-24.64, 4.89) * mm, "end": v(-23.36, 4.63) * mm});
            skLineSegment(sketch, "E2.79.1", {"start": v(-24.6, 5.14) * mm, "end": v(-23.31, 4.87) * mm});
            skLineSegment(sketch, "E2.79.2", {"start": v(-23.36, 4.63) * mm, "end": v(-23.31, 4.87) * mm});
            skLineSegment(sketch, "E2.79.3", {"start": v(-24.64, 4.89) * mm, "end": v(-24.6, 5.14) * mm});
            skLineSegment(sketch, "E2.80.0", {"start": v(-24.3, 6.4) * mm, "end": v(-23.03, 6.07) * mm});
            skLineSegment(sketch, "E2.80.1", {"start": v(-24.23, 6.65) * mm, "end": v(-22.96, 6.31) * mm});
            skLineSegment(sketch, "E2.80.2", {"start": v(-23.03, 6.07) * mm, "end": v(-22.96, 6.31) * mm});
            skLineSegment(sketch, "E2.80.3", {"start": v(-24.3, 6.4) * mm, "end": v(-24.23, 6.65) * mm});
            skLineSegment(sketch, "E2.81.0", {"start": v(-23.85, 7.9) * mm, "end": v(-22.6, 7.49) * mm});
            skLineSegment(sketch, "E2.81.1", {"start": v(-23.76, 8.15) * mm, "end": v(-22.53, 7.73) * mm});
            skLineSegment(sketch, "E2.81.2", {"start": v(-22.6, 7.49) * mm, "end": v(-22.53, 7.73) * mm});
            skLineSegment(sketch, "E2.81.3", {"start": v(-23.85, 7.9) * mm, "end": v(-23.76, 8.15) * mm});
            skLineSegment(sketch, "E2.82.0", {"start": v(-23.3, 9.37) * mm, "end": v(-22.1, 8.88) * mm});
            skLineSegment(sketch, "E2.82.1", {"start": v(-23.21, 9.6) * mm, "end": v(-22, 9.11) * mm});
            skLineSegment(sketch, "E2.82.2", {"start": v(-22.1, 8.88) * mm, "end": v(-22, 9.11) * mm});
            skLineSegment(sketch, "E2.82.3", {"start": v(-23.3, 9.37) * mm, "end": v(-23.21, 9.6) * mm});
            skLineSegment(sketch, "E2.83.0", {"start": v(-22.68, 10.8) * mm, "end": v(-21.5, 10.24) * mm});
            skLineSegment(sketch, "E2.83.1", {"start": v(-22.57, 11.03) * mm, "end": v(-21.4, 10.46) * mm});
            skLineSegment(sketch, "E2.83.2", {"start": v(-21.5, 10.24) * mm, "end": v(-21.4, 10.46) * mm});
            skLineSegment(sketch, "E2.83.3", {"start": v(-22.68, 10.8) * mm, "end": v(-22.57, 11.03) * mm});
            skLineSegment(sketch, "E2.84.0", {"start": v(-21.97, 12.2) * mm, "end": v(-20.83, 11.55) * mm});
            skLineSegment(sketch, "E2.84.1", {"start": v(-21.84, 12.41) * mm, "end": v(-20.7, 11.77) * mm});
            skLineSegment(sketch, "E2.84.2", {"start": v(-20.83, 11.55) * mm, "end": v(-20.7, 11.77) * mm});
            skLineSegment(sketch, "E2.84.3", {"start": v(-21.97, 12.2) * mm, "end": v(-21.84, 12.41) * mm});
            skLineSegment(sketch, "E2.85.0", {"start": v(-21.17, 13.53) * mm, "end": v(-20.07, 12.82) * mm});
            skLineSegment(sketch, "E2.85.1", {"start": v(-21.03, 13.75) * mm, "end": v(-19.93, 13.04) * mm});
            skLineSegment(sketch, "E2.85.2", {"start": v(-20.07, 12.82) * mm, "end": v(-19.93, 13.04) * mm});
            skLineSegment(sketch, "E2.85.3", {"start": v(-21.17, 13.53) * mm, "end": v(-21.03, 13.75) * mm});
            skLineSegment(sketch, "E2.86.0", {"start": v(-20.28, 14.82) * mm, "end": v(-19.23, 14.05) * mm});
            skLineSegment(sketch, "E2.86.1", {"start": v(-20.13, 15.03) * mm, "end": v(-19.08, 14.25) * mm});
            skLineSegment(sketch, "E2.86.2", {"start": v(-19.23, 14.05) * mm, "end": v(-19.08, 14.25) * mm});
            skLineSegment(sketch, "E2.86.3", {"start": v(-20.28, 14.82) * mm, "end": v(-20.13, 15.03) * mm});
            skLineSegment(sketch, "E2.87.0", {"start": v(-19.32, 16.06) * mm, "end": v(-18.32, 15.21) * mm});
            skLineSegment(sketch, "E2.87.1", {"start": v(-19.16, 16.25) * mm, "end": v(-18.16, 15.4) * mm});
            skLineSegment(sketch, "E2.87.2", {"start": v(-18.32, 15.21) * mm, "end": v(-18.16, 15.4) * mm});
            skLineSegment(sketch, "E2.87.3", {"start": v(-19.32, 16.06) * mm, "end": v(-19.16, 16.25) * mm});
            skLineSegment(sketch, "E2.88.0", {"start": v(-18.29, 17.23) * mm, "end": v(-17.34, 16.32) * mm});
            skLineSegment(sketch, "E2.88.1", {"start": v(-18.11, 17.4) * mm, "end": v(-17.17, 16.5) * mm});
            skLineSegment(sketch, "E2.88.2", {"start": v(-17.34, 16.32) * mm, "end": v(-17.17, 16.5) * mm});
            skLineSegment(sketch, "E2.88.3", {"start": v(-18.29, 17.23) * mm, "end": v(-18.11, 17.4) * mm});
            skLineSegment(sketch, "E2.89.0", {"start": v(-17.18, 18.33) * mm, "end": v(-16.3, 17.37) * mm});
            skLineSegment(sketch, "E2.89.1", {"start": v(-17, 18.5) * mm, "end": v(-16.1, 17.54) * mm});
            skLineSegment(sketch, "E2.89.2", {"start": v(-16.3, 17.37) * mm, "end": v(-16.1, 17.54) * mm});
            skLineSegment(sketch, "E2.89.3", {"start": v(-17.18, 18.33) * mm, "end": v(-17, 18.5) * mm});
            skLineSegment(sketch, "E2.90.0", {"start": v(-16, 19.36) * mm, "end": v(-15.18, 18.35) * mm});
            skLineSegment(sketch, "E2.90.1", {"start": v(-15.81, 19.52) * mm, "end": v(-14.98, 18.51) * mm});
            skLineSegment(sketch, "E2.90.2", {"start": v(-15.18, 18.35) * mm, "end": v(-14.98, 18.51) * mm});
            skLineSegment(sketch, "E2.90.3", {"start": v(-16, 19.36) * mm, "end": v(-15.81, 19.52) * mm});
            skLineSegment(sketch, "E2.91.0", {"start": v(-14.77, 20.32) * mm, "end": v(-14.01, 19.26) * mm});
            skLineSegment(sketch, "E2.91.1", {"start": v(-14.57, 20.47) * mm, "end": v(-13.8, 19.4) * mm});
            skLineSegment(sketch, "E2.91.2", {"start": v(-14.01, 19.26) * mm, "end": v(-13.8, 19.4) * mm});
            skLineSegment(sketch, "E2.91.3", {"start": v(-14.77, 20.32) * mm, "end": v(-14.57, 20.47) * mm});
            skLineSegment(sketch, "E2.92.0", {"start": v(-13.48, 21.2) * mm, "end": v(-12.79, 20.1) * mm});
            skLineSegment(sketch, "E2.92.1", {"start": v(-13.27, 21.33) * mm, "end": v(-12.57, 20.23) * mm});
            skLineSegment(sketch, "E2.92.2", {"start": v(-12.79, 20.1) * mm, "end": v(-12.57, 20.23) * mm});
            skLineSegment(sketch, "E2.92.3", {"start": v(-13.48, 21.2) * mm, "end": v(-13.27, 21.33) * mm});
            skLineSegment(sketch, "E2.93.0", {"start": v(-12.14, 22) * mm, "end": v(-11.51, 20.85) * mm});
            skLineSegment(sketch, "E2.93.1", {"start": v(-11.92, 22.12) * mm, "end": v(-11.3, 20.97) * mm});
            skLineSegment(sketch, "E2.93.2", {"start": v(-11.51, 20.85) * mm, "end": v(-11.3, 20.97) * mm});
            skLineSegment(sketch, "E2.93.3", {"start": v(-12.14, 22) * mm, "end": v(-11.92, 22.12) * mm});
            skLineSegment(sketch, "E2.94.0", {"start": v(-10.75, 22.7) * mm, "end": v(-10.2, 21.52) * mm});
            skLineSegment(sketch, "E2.94.1", {"start": v(-10.52, 22.81) * mm, "end": v(-9.97, 21.63) * mm});
            skLineSegment(sketch, "E2.94.2", {"start": v(-10.2, 21.52) * mm, "end": v(-9.97, 21.63) * mm});
            skLineSegment(sketch, "E2.94.3", {"start": v(-10.75, 22.7) * mm, "end": v(-10.52, 22.81) * mm});
            skLineSegment(sketch, "E2.95.0", {"start": v(-9.32, 23.33) * mm, "end": v(-8.84, 22.11) * mm});
            skLineSegment(sketch, "E2.95.1", {"start": v(-9.08, 23.42) * mm, "end": v(-8.6, 22.2) * mm});
            skLineSegment(sketch, "E2.95.2", {"start": v(-8.84, 22.11) * mm, "end": v(-8.6, 22.2) * mm});
            skLineSegment(sketch, "E2.95.3", {"start": v(-9.32, 23.33) * mm, "end": v(-9.08, 23.42) * mm});
            skLineSegment(sketch, "E2.96.0", {"start": v(-7.85, 23.86) * mm, "end": v(-7.45, 22.62) * mm});
            skLineSegment(sketch, "E2.96.1", {"start": v(-7.6, 23.94) * mm, "end": v(-7.2, 22.7) * mm});
            skLineSegment(sketch, "E2.96.2", {"start": v(-7.45, 22.62) * mm, "end": v(-7.2, 22.7) * mm});
            skLineSegment(sketch, "E2.96.3", {"start": v(-7.85, 23.86) * mm, "end": v(-7.6, 23.94) * mm});
            skLineSegment(sketch, "E2.97.0", {"start": v(-6.35, 24.3) * mm, "end": v(-6.03, 23.04) * mm});
            skLineSegment(sketch, "E2.97.1", {"start": v(-6.1, 24.37) * mm, "end": v(-5.78, 23.1) * mm});
            skLineSegment(sketch, "E2.97.2", {"start": v(-6.03, 23.04) * mm, "end": v(-5.78, 23.1) * mm});
            skLineSegment(sketch, "E2.97.3", {"start": v(-6.35, 24.3) * mm, "end": v(-6.1, 24.37) * mm});
            skLineSegment(sketch, "E2.98.0", {"start": v(-4.83, 24.65) * mm, "end": v(-4.58, 23.37) * mm});
            skLineSegment(sketch, "E2.98.1", {"start": v(-4.58, 24.7) * mm, "end": v(-4.33, 23.42) * mm});
            skLineSegment(sketch, "E2.98.2", {"start": v(-4.58, 23.37) * mm, "end": v(-4.33, 23.42) * mm});
            skLineSegment(sketch, "E2.98.3", {"start": v(-4.83, 24.65) * mm, "end": v(-4.58, 24.7) * mm});
            skLineSegment(sketch, "E2.99.0", {"start": v(-3.29, 24.9) * mm, "end": v(-3.12, 23.6) * mm});
            skLineSegment(sketch, "E2.99.1", {"start": v(-3.03, 24.94) * mm, "end": v(-2.87, 23.64) * mm});
            skLineSegment(sketch, "E2.99.2", {"start": v(-3.12, 23.6) * mm, "end": v(-2.87, 23.64) * mm});
            skLineSegment(sketch, "E2.99.3", {"start": v(-3.29, 24.9) * mm, "end": v(-3.03, 24.94) * mm});
            skLineSegment(sketch, "E2.100.0", {"start": v(-1.73, 25.06) * mm, "end": v(-1.65, 23.76) * mm});
            skLineSegment(sketch, "E2.100.1", {"start": v(-1.48, 25.08) * mm, "end": v(-1.4, 23.77) * mm});
            skLineSegment(sketch, "E2.100.2", {"start": v(-1.65, 23.76) * mm, "end": v(-1.4, 23.77) * mm});
            skLineSegment(sketch, "E2.100.3", {"start": v(-1.73, 25.06) * mm, "end": v(-1.48, 25.08) * mm});
            skPoint(sketch, "E2.center", {"position": v(0, 0) * mm});
            skLineSegment(sketch, "E2.anchor1", {"start": v(0, 0) * mm, "end": v(-0.13, 23.82) * mm, "construction": true});
            skLineSegment(sketch, "E2.anchor2", {"start": v(0, 0) * mm, "end": v(-0.16, 23.3) * mm, "construction": true});
            skPoint(sketch, "E3.orphan", {"position": v(0.09, 23.82) * mm});
            skPoint(sketch, "E4.orphan", {"position": v(-0.17, 25.12) * mm});
            skLineSegment(sketch, "E5", {"start": v(-0.13, 23.82) * mm, "end": v(0.13, 23.82) * mm});
            skLineSegment(sketch, "E6", {"start": v(-0.13, 25.12) * mm, "end": v(0.13, 25.12) * mm});
            skSolve(sketch);
        }
        {
            var Q0;
            Q0 = qSketchRegion(id + "F3", true);
            extrude(context, id + "F4", {"entities" : qUnion([Q0]), "operationType" : NewBodyOperationType.REMOVE, "endBound" : BoundingType.THROUGH_ALL, "oppositeDirection" : true, "depth" : 25.4 * mm});
        }
    });
